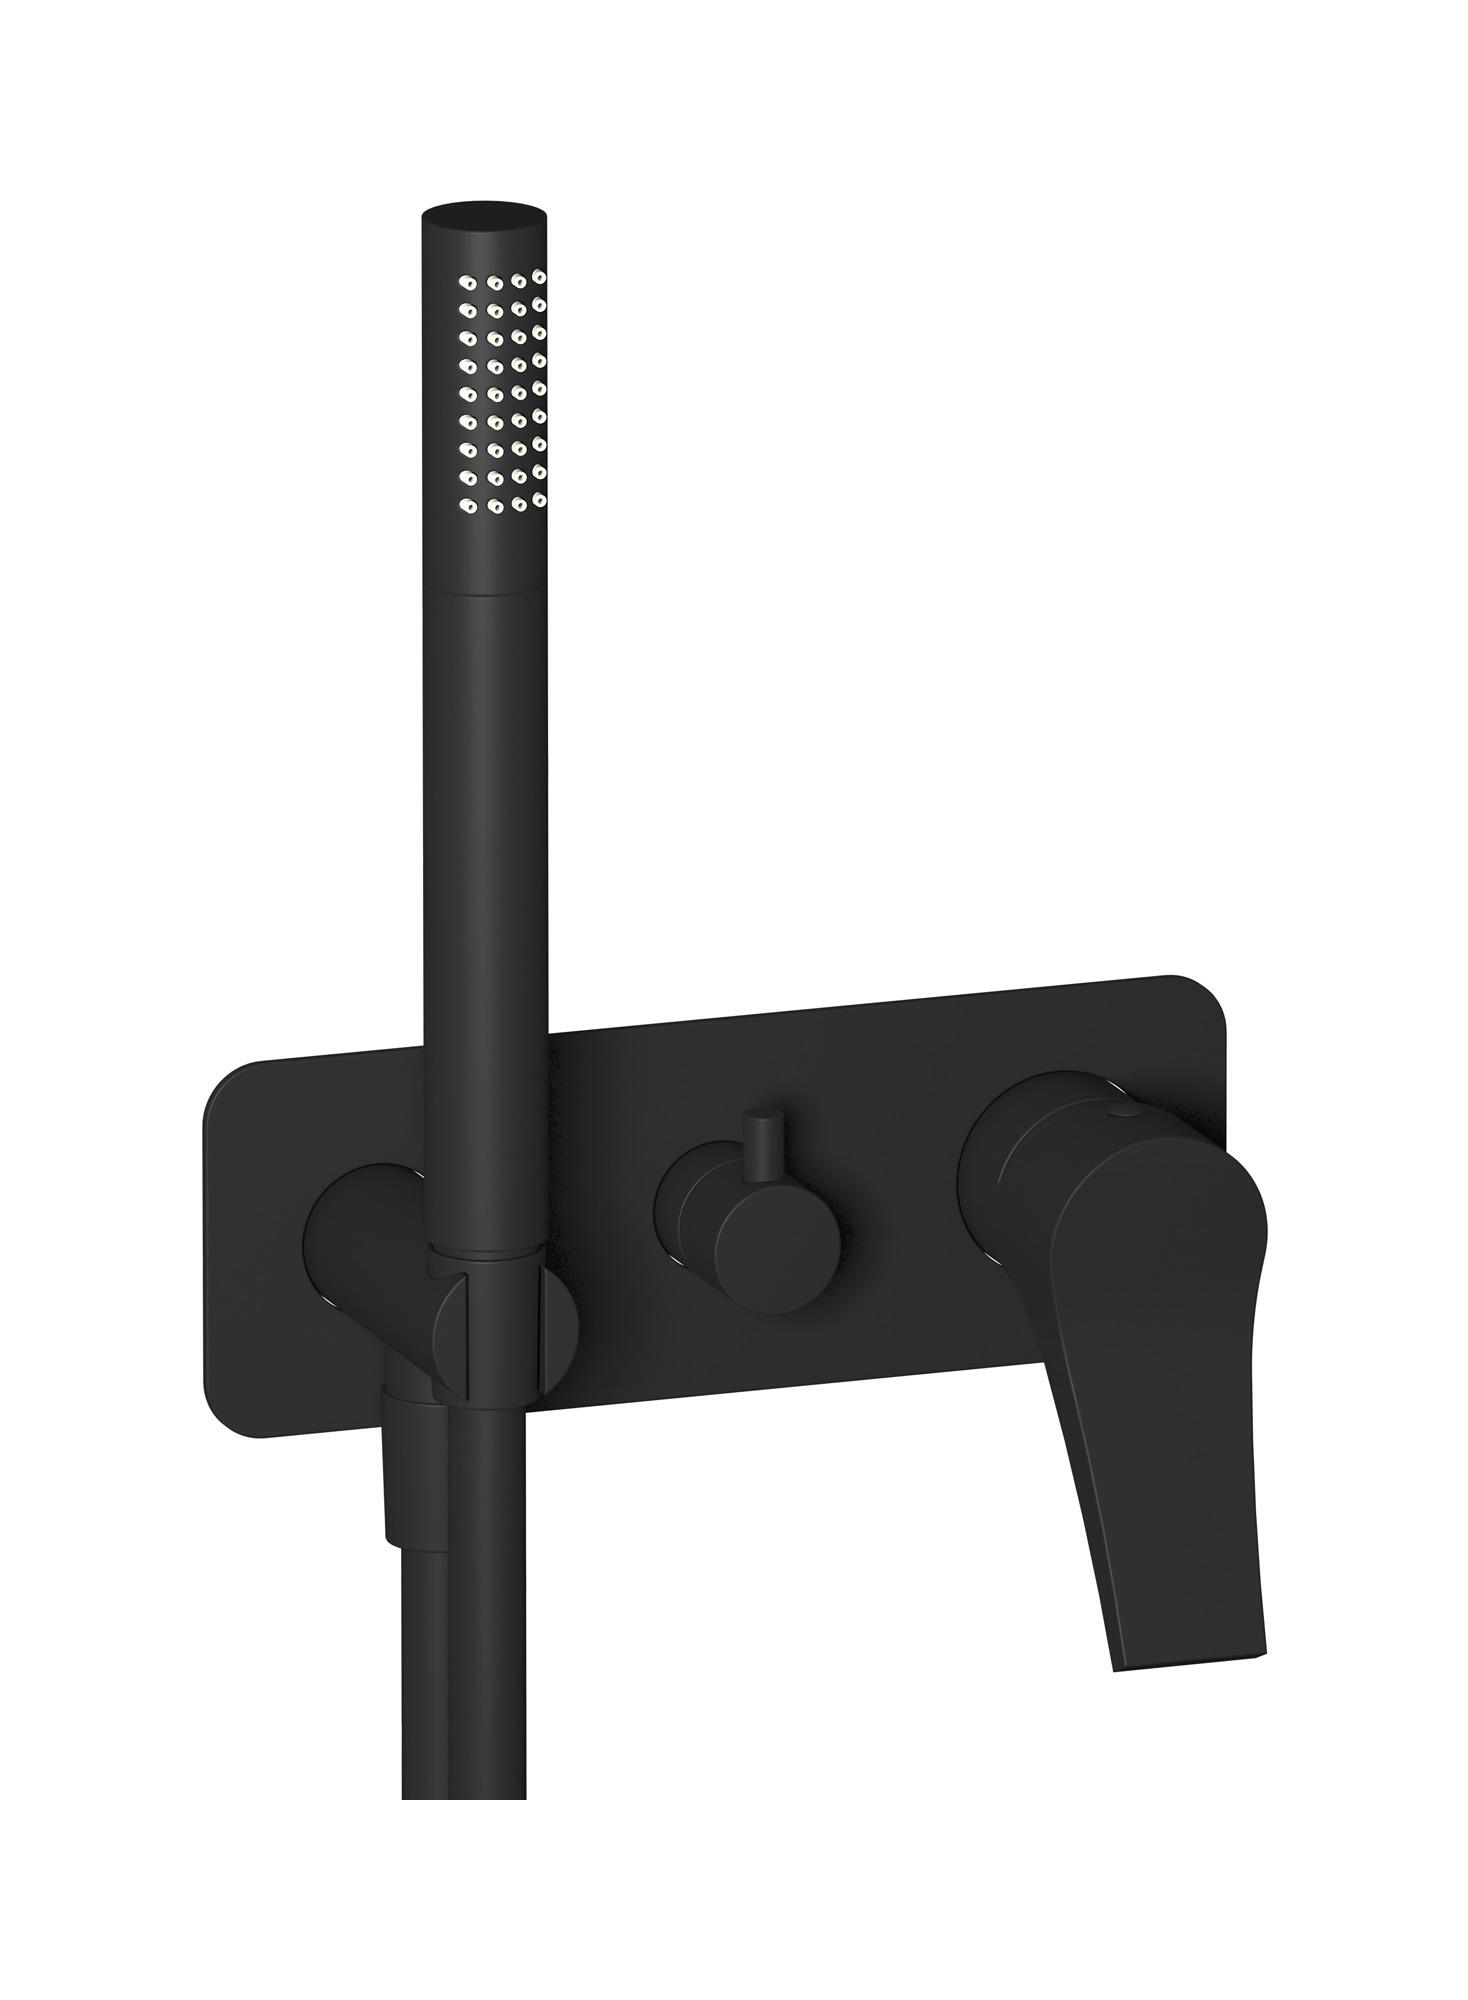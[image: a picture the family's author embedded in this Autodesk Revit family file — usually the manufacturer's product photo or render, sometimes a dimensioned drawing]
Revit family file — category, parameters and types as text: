
# Revit family: TW314
name_source: partatom
category: Apparecchi idraulici
units: mm (PartAtom-declared; Revit-internal decimal feet)

## family parameters
Basato su piano di lavoro = No
Condiviso = No
Mantieni orientamento annotazione = No
Numero OmniClass = 23.45.55.17
Punto di calcolo locali = No
Quota connettore circolare = Usa diametro
Sempre verticale = Sì
Taglio con vuoti quando caricato = No
Tipo di parte = Normale
Titolo OmniClass = Mixing Faucets

## types (12) — shared parameters
Cold water inlet = 10 mm  [stored 0.0328084 ft]
Commenti sul tipo = Wall mixer
Connessione CW = No
Connessione HW = No
Connessione di scarico = No
Connessione di ventilazione = No
Descrizione = Exposed parts for manual wall mixer with three ways diverter and shower kit
Hot water inlet = 10 mm  [stored 0.0328084 ft]
Produttore = IB Rubinetterie S.p.A.
URL = https://www.weareib.it
zero-valued in all types: Prospetto di default

## per-type parameters (varying)
| type | Finishes surface | Immagine tipo | Modello |
| Chrome | IB_Chrome | TW314CC.jpg | TW314CC |
| Brushed nickel | IB_Brushed nickel | TW314SS.jpg | TW314SS |
| Matt black | IB_matt black | TW314NP.jpg | TW314NP |
| Matt white | IB_matt white | TW314BO.jpg | TW314BO |
| Black chrome | IB_Black chrome | TW314CF.jpg | TW314CF |
| Brushed black chrome | IB_Brushed black chrome | TW314CS.jpg | TW314CS |
| Pale gold | IB_Pale gold | TW314II.jpg | TW314II |
| Brushed pale gold | IB_brushed pale gold | TW314IS.jpg | TW314IS |
| Rose gold | IB_Rose gold | TW314RS.jpg | TW314RS |
| Brushed rose gold | IB_Brushed rose gold | TW314SR.jpg | TW314SR |
| Gold | IB_gold | TW314OO.jpg | TW314OO |
| Brushed gold | IB_brushed gold | TW314OS.jpg | TW314OS |

note: [stored X ft] marks values corroborated as IEEE doubles in the binary element streams (Revit-internal decimal feet)
